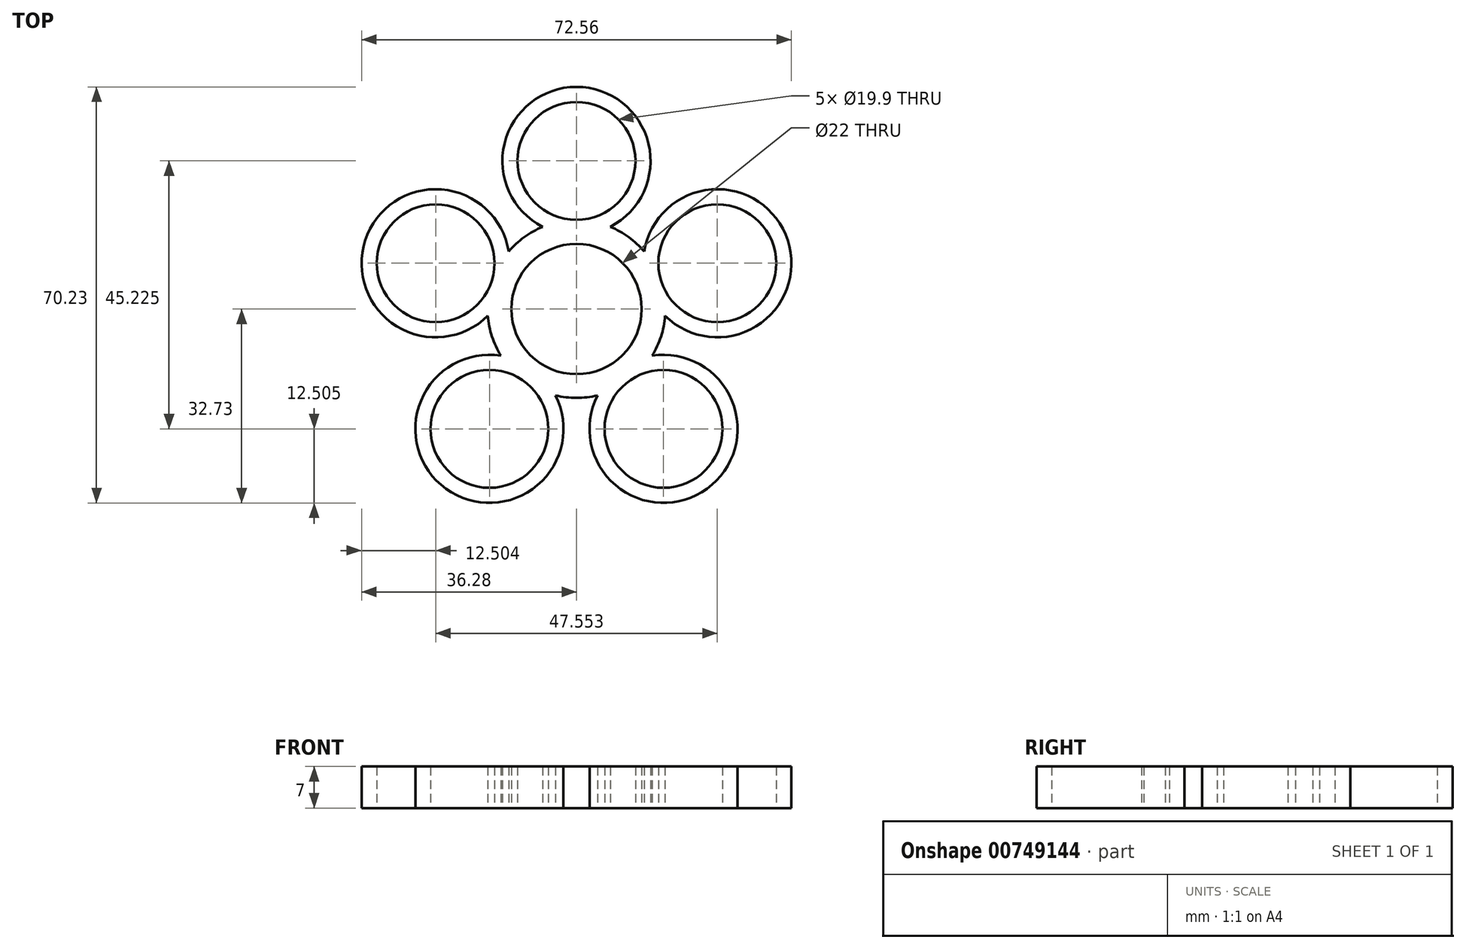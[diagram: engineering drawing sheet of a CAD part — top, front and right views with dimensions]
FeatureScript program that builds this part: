
annotation { "Feature Type Name" : "Feature", "Feature Type Description" : "" }
export const myFeature = defineFeature(function(context is Context, id is Id, definition is map)
    precondition{}
    {
        {
            var Q0;
            Q0=qCreatedBy(makeId("Top.planeOp"),FACE);
            var sketch = newSketch(context, id + "F0", { "sketchPlane" : qUnion([Q0])});
            skArc(sketch, "E0", {"start": v(6.47, 8.9) * mm, "mid": v(0, 11) * mm, "end": v(-6.47, 8.9) * mm});
            skArc(sketch, "E1", {"start": v(8.82, 12.14) * mm, "mid": v(7.31, 13.1) * mm, "end": v(5.7, 13.88) * mm});
            skCircle(sketch, "E2", {"center": v(0, 25) * mm, "radius": 9.95 * mm});
            skArc(sketch, "E3", {"start": v(5.7, 13.88) * mm, "mid": v(0, 37.5) * mm, "end": v(-5.7, 13.88) * mm});
            skArc(sketch, "E4.MirrorCS", {"start": v(6.47, 8.9) * mm, "mid": v(10.46, 3.4) * mm, "end": v(10.46, -3.4) * mm});
            skArc(sketch, "E5.MirrorCS", {"start": v(8.82, 12.14) * mm, "mid": v(10.2, 11) * mm, "end": v(11.43, 9.7) * mm});
            skCircle(sketch, "E6.MirrorC", {"center": v(23.78, 7.73) * mm, "radius": 9.95 * mm});
            skArc(sketch, "E7.MirrorC", {"start": v(11.43, 9.7) * mm, "mid": v(35.66, 11.59) * mm, "end": v(14.96, -1.13) * mm});
            skArc(sketch, "E8.MirrorCS", {"start": v(-14.27, -4.64) * mm, "mid": v(-14.72, -2.9) * mm, "end": v(-14.96, -1.13) * mm});
            skArc(sketch, "E9.MirrorCS", {"start": v(-10.46, -3.4) * mm, "mid": v(-10.46, 3.4) * mm, "end": v(-6.47, 8.9) * mm});
            skCircle(sketch, "E10.MirrorC", {"center": v(-23.78, 7.73) * mm, "radius": 9.95 * mm});
            skArc(sketch, "E11.MirrorC", {"start": v(-14.96, -1.13) * mm, "mid": v(-35.66, 11.59) * mm, "end": v(-11.43, 9.7) * mm});
            skArc(sketch, "E12.MirrorCS", {"start": v(0, -11) * mm, "mid": v(6.47, -8.9) * mm, "end": v(10.46, -3.4) * mm});
            skArc(sketch, "E13.MirrorCS", {"start": v(0, -15) * mm, "mid": v(1.78, -14.9) * mm, "end": v(3.54, -14.58) * mm});
            skCircle(sketch, "E14.MirrorC", {"center": v(14.7, -20.23) * mm, "radius": 9.95 * mm});
            skArc(sketch, "E15.MirrorC", {"start": v(3.54, -14.58) * mm, "mid": v(22.04, -30.34) * mm, "end": v(12.77, -7.88) * mm});
            skCircle(sketch, "E16.MirrorC", {"center": v(-14.7, -20.23) * mm, "radius": 9.95 * mm});
            skArc(sketch, "E17.MirrorC", {"start": v(-3.54, -14.58) * mm, "mid": v(-22.04, -30.34) * mm, "end": v(-12.77, -7.88) * mm});
            skArc(sketch, "E18.MirrorCS", {"start": v(0, -15) * mm, "mid": v(-1.78, -14.9) * mm, "end": v(-3.54, -14.58) * mm});
            skArc(sketch, "E19.MirrorCS", {"start": v(0, -11) * mm, "mid": v(-6.47, -8.9) * mm, "end": v(-10.46, -3.4) * mm});
            skArc(sketch, "E20.trimOffspring", {"start": v(-5.7, 13.87) * mm, "mid": v(-7.31, 13.1) * mm, "end": v(-8.82, 12.14) * mm});
            skArc(sketch, "E21.trimOffspring", {"start": v(14.96, -1.13) * mm, "mid": v(14.72, -2.9) * mm, "end": v(14.27, -4.64) * mm});
            skArc(sketch, "E22.trimOffspring", {"start": v(-11.43, 9.7) * mm, "mid": v(-10.2, 11) * mm, "end": v(-8.82, 12.14) * mm});
            skArc(sketch, "E23.trimOffspring", {"start": v(-12.77, -7.88) * mm, "mid": v(-13.61, -6.3) * mm, "end": v(-14.27, -4.64) * mm});
            skArc(sketch, "E24.trimOffspring", {"start": v(12.77, -7.88) * mm, "mid": v(13.61, -6.3) * mm, "end": v(14.27, -4.64) * mm});
            skSolve(sketch);
        }
        {
            var Q0;
            Q0 = qSketchRegion(id + "F0", true);
            extrude(context, id + "F1", {"entities" : qUnion([Q0]), "depth" : 7 * mm, "offsetDistance" : 25 * mm});
        }
    });
